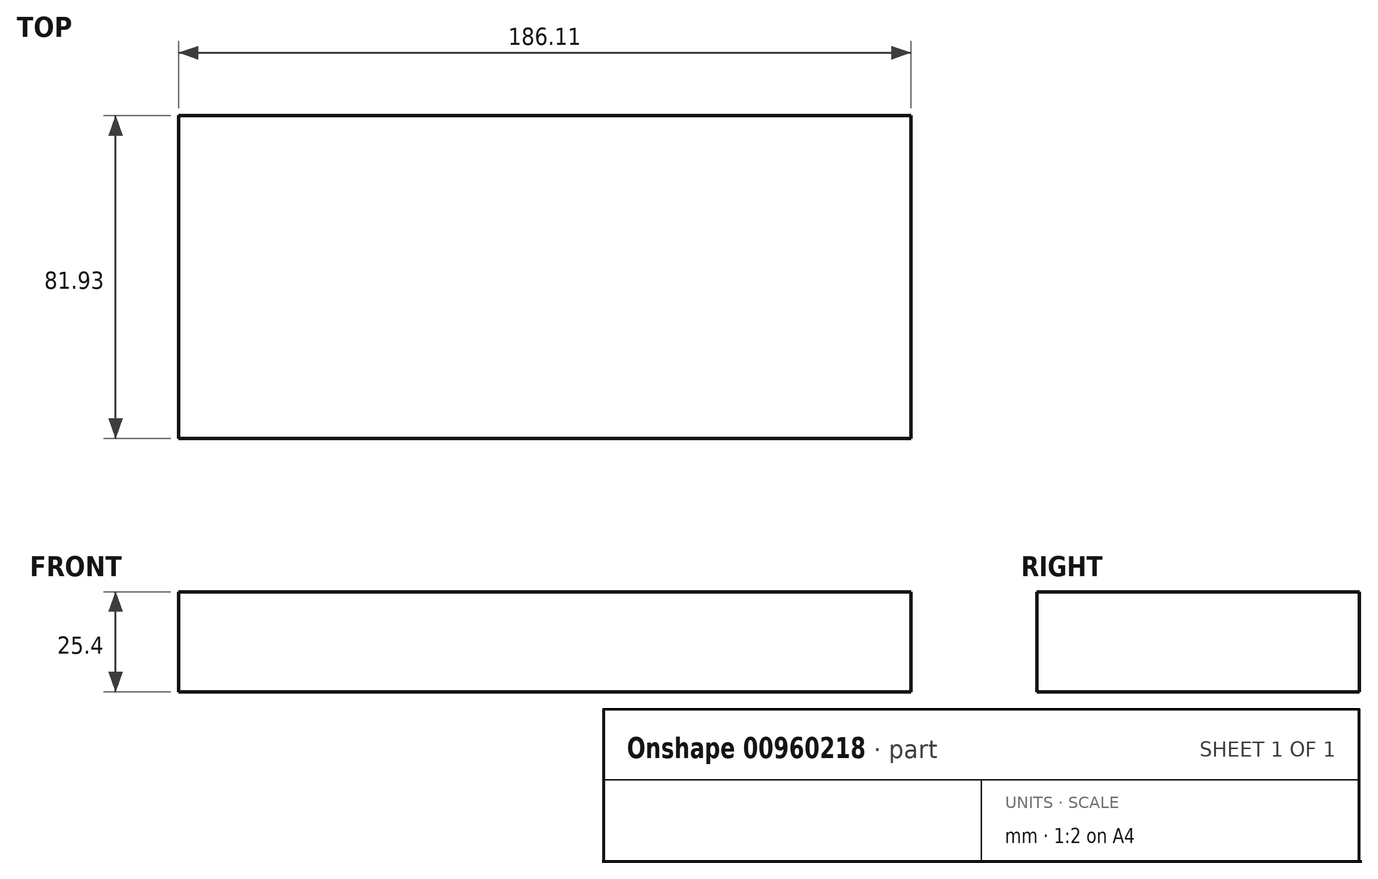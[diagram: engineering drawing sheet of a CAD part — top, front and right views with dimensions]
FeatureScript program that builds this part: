
annotation { "Feature Type Name" : "Feature", "Feature Type Description" : "" }
export const myFeature = defineFeature(function(context is Context, id is Id, definition is map)
    precondition{}
    {
        {
            var Q0;
            Q0=qCreatedBy(makeId("Top.planeOp"),FACE);
            var sketch = newSketch(context, id + "F0", { "sketchPlane" : qUnion([Q0])});
            skLineSegment(sketch, "E0.bottom", {"start": v(-70.55, 41.59) * mm, "end": v(115.56, 41.59) * mm});
            skLineSegment(sketch, "E0.top", {"start": v(-70.55, -40.34) * mm, "end": v(115.56, -40.34) * mm});
            skLineSegment(sketch, "E0.left", {"start": v(-70.55, 41.59) * mm, "end": v(-70.55, -40.34) * mm});
            skLineSegment(sketch, "E0.right", {"start": v(115.56, 41.59) * mm, "end": v(115.56, -40.34) * mm});
            skSolve(sketch);
        }
        {
            var Q0;
            Q0=makeQuery(id+"F0.imprint","IMPRINT",FACE,{"disambiguationData":[TD([[makeQuery(id+"F0.imprint","IMPRINT",EDGE,{"derivedFrom":sQuery(id+"F0.wireOp",EDGE,"E0.bottom")}),-1.0]])]});
            extrude(context, id + "F1", {"entities" : qUnion([Q0]), "depth" : 25.4 * mm, "offsetDistance" : 25.4 * mm});
        }
    });
